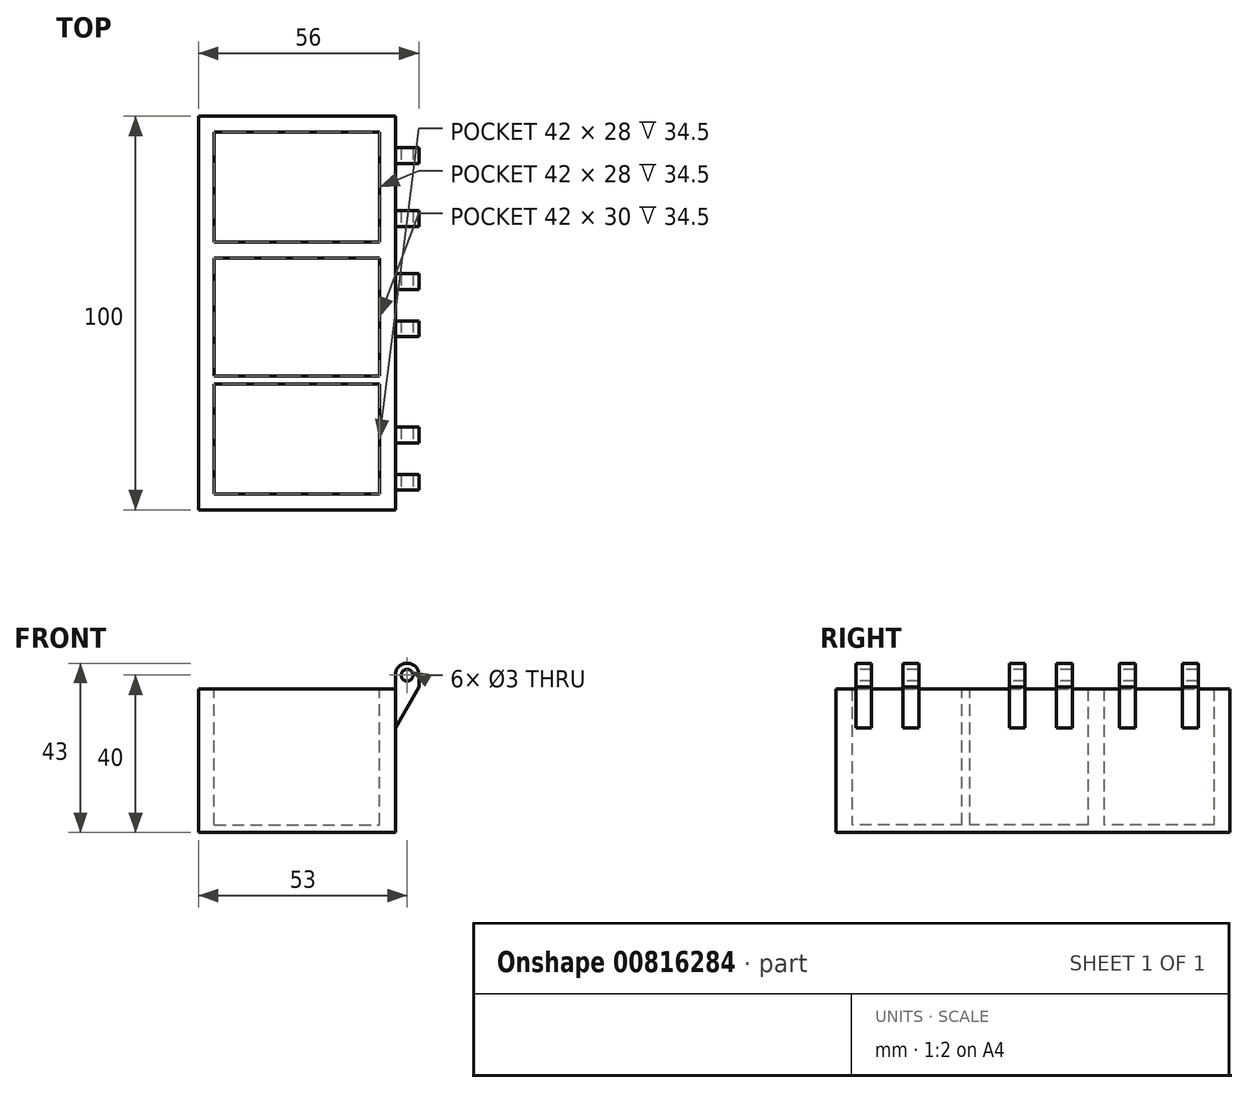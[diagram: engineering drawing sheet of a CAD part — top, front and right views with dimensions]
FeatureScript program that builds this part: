
annotation { "Feature Type Name" : "Feature", "Feature Type Description" : "" }
export const myFeature = defineFeature(function(context is Context, id is Id, definition is map)
    precondition{}
    {
        {
            var Q0;
            Q0=qCreatedBy(makeId("Top.planeOp"),FACE);
            var sketch = newSketch(context, id + "F0", { "sketchPlane" : qUnion([Q0])});
            skLineSegment(sketch, "E0.bottom", {"start": v(0, 0) * mm, "end": v(50, 0) * mm});
            skLineSegment(sketch, "E0.top", {"start": v(0, 100) * mm, "end": v(50, 100) * mm});
            skLineSegment(sketch, "E0.left", {"start": v(0, 0) * mm, "end": v(0, 100) * mm});
            skLineSegment(sketch, "E0.right", {"start": v(50, 0) * mm, "end": v(50, 100) * mm});
            skLineSegment(sketch, "E1.bottom", {"start": v(4, 96) * mm, "end": v(46, 96) * mm});
            skLineSegment(sketch, "E1.top", {"start": v(4, 68) * mm, "end": v(46, 68) * mm});
            skLineSegment(sketch, "E1.left", {"start": v(4, 96) * mm, "end": v(4, 68) * mm});
            skLineSegment(sketch, "E1.right", {"start": v(46, 96) * mm, "end": v(46, 68) * mm});
            skLineSegment(sketch, "E2.bottom", {"start": v(4, 64) * mm, "end": v(46, 64) * mm});
            skLineSegment(sketch, "E2.top", {"start": v(4, 4) * mm, "end": v(46, 4) * mm});
            skLineSegment(sketch, "E2.left", {"start": v(4, 64) * mm, "end": v(4, 4) * mm});
            skLineSegment(sketch, "E2.right", {"start": v(46, 64) * mm, "end": v(46, 4) * mm});
            skSolve(sketch);
        }
        {
            var Q0;
            Q0 = qSketchRegion(id + "F0", true);
            extrude(context, id + "F1", {"entities" : qUnion([Q0]), "depth" : 35 * mm, "offsetDistance" : 25 * mm});
        }
        {
            var Q0;
            Q0=makeQuery(id+"F1.opExtrude","CAP_FACE",FACE,{"disambiguationData":[OSD([sQuery(id+"F0.wireOp",EDGE,"E0.bottom"),sQuery(id+"F0.wireOp",EDGE,"E0.top"),sQuery(id+"F0.wireOp",EDGE,"E0.left"),sQuery(id+"F0.wireOp",EDGE,"E0.right"),sQuery(id+"F0.wireOp",EDGE,"E1.bottom"),sQuery(id+"F0.wireOp",EDGE,"E1.top"),sQuery(id+"F0.wireOp",EDGE,"E1.left"),sQuery(id+"F0.wireOp",EDGE,"E1.right"),sQuery(id+"F0.wireOp",EDGE,"E2.bottom"),sQuery(id+"F0.wireOp",EDGE,"E2.top"),sQuery(id+"F0.wireOp",EDGE,"E2.left"),sQuery(id+"F0.wireOp",EDGE,"E2.right")])],"isStart":true});
            var sketch = newSketch(context, id + "F2", { "sketchPlane" : qUnion([Q0])});
            skLineSegment(sketch, "E3.bottom", {"start": v(50, -100) * mm, "end": v(0, -100) * mm});
            skLineSegment(sketch, "E3.top", {"start": v(50, 0) * mm, "end": v(0, 0) * mm});
            skLineSegment(sketch, "E3.left", {"start": v(50, -100) * mm, "end": v(50, 0) * mm});
            skLineSegment(sketch, "E3.right", {"start": v(0, -100) * mm, "end": v(0, 0) * mm});
            skSolve(sketch);
        }
        {
            var Q0;
            Q0 = qSketchRegion(id + "F2", true);
            extrude(context, id + "F3", {"entities" : qUnion([Q0]), "operationType" : NewBodyOperationType.ADD, "depth" : 2 * mm, "offsetDistance" : 25 * mm});
        }
        {
            var Q0;
            Q0=makeQuery(id+"F3.boolean.opBoolean","MERGE",FACE,{"derivedFrom":[makeQuery(id+"F1.opExtrude","SWEPT_FACE",FACE,{"disambiguationData":[OSD([sQuery(id+"F0.wireOp",EDGE,"E0.bottom")])]}),makeQuery(id+"F3.opExtrude","SWEPT_FACE",FACE,{"disambiguationData":[OSD([sQuery(id+"F2.wireOp",EDGE,"E3.top")])]})]});
            var sketch = newSketch(context, id + "F4", { "sketchPlane" : qUnion([Q0])});
            skLineSegment(sketch, "E4", {"start": v(50, 24.6) * mm, "end": v(56, 35) * mm});
            skLineSegment(sketch, "E5", {"start": v(56, 35) * mm, "end": v(56, 41) * mm});
            skLineSegment(sketch, "E6", {"start": v(56, 41) * mm, "end": v(50, 41) * mm});
            skLineSegment(sketch, "E7", {"start": v(50, 41) * mm, "end": v(50, 35) * mm});
            skCircle(sketch, "E8", {"center": v(53, 38) * mm, "radius": 1.5 * mm});
            skLineSegment(sketch, "E9", {"start": v(50, 41) * mm, "end": v(56, 35) * mm, "construction": true});
            skLineSegment(sketch, "E10", {"start": v(50, 35) * mm, "end": v(56, 35) * mm, "construction": true});
            skSolve(sketch);
        }
        {
            var Q0;
            {var subQ1=sQuery(id+"F4.wireOp",EDGE,"E4");Q0=makeQuery(id+"F4.imprint","IMPRINT",FACE,{"disambiguationData":[TD([[makeQuery(id+"F4.imprint","IMPRINT",EDGE,{"derivedFrom":subQ1}),1.0]])]});}
            var Q1;
            Q1=makeQuery(id+"F3.boolean.opBoolean","MERGE",FACE,{"derivedFrom":[makeQuery(id+"F1.opExtrude","SWEPT_FACE",FACE,{"disambiguationData":[OSD([sQuery(id+"F0.wireOp",EDGE,"E0.top")])]}),makeQuery(id+"F3.opExtrude","SWEPT_FACE",FACE,{"disambiguationData":[OSD([sQuery(id+"F2.wireOp",EDGE,"E3.bottom")])]})]});
            extrude(context, id + "F5", {"entities" : qUnion([Q0]), "operationType" : NewBodyOperationType.ADD, "endBound" : BoundingType.UP_TO_SURFACE, "oppositeDirection" : true, "depth" : 25 * mm, "endBoundEntityFace" : qUnion([Q1]), "offsetDistance" : 25 * mm});
        }
        {
            var Q0;
            Q0=makeQuery(id+"F5.opExtrude","SWEPT_EDGE",EDGE,{"disambiguationData":[OSD([sQuery(id+"F4.wireOp",EDGE,"E5"),sQuery(id+"F4.wireOp",EDGE,"E6")])]});
            var Q1;
            Q1=makeQuery(id+"F5.opExtrude","SWEPT_EDGE",EDGE,{"disambiguationData":[OSD([sQuery(id+"F4.wireOp",EDGE,"E6"),sQuery(id+"F4.wireOp",EDGE,"E7")])]});
            fillet(context, id + "F6", {"entities" : qUnion([Q0, Q1]), "radius" : (5.7 / 2) * mm, "tangentPropagation" : true, "allowEdgeOverflow" : false});
        }
        {
            var Q0;
            Q0=makeQuery(id+"F3.opExtrude","CAP_FACE",FACE,{"disambiguationData":[OSD([sQuery(id+"F2.wireOp",EDGE,"E3.bottom"),sQuery(id+"F2.wireOp",EDGE,"E3.top"),sQuery(id+"F2.wireOp",EDGE,"E3.left"),sQuery(id+"F2.wireOp",EDGE,"E3.right")])],"isStart":false});
            var sketch = newSketch(context, id + "F7", { "sketchPlane" : qUnion([Q0])});
            skLineSegment(sketch, "E11.bottom", {"start": v(50, 0) * mm, "end": v(65, 0) * mm});
            skLineSegment(sketch, "E11.top", {"start": v(50, -5) * mm, "end": v(65, -5) * mm});
            skLineSegment(sketch, "E11.left", {"start": v(50, 0) * mm, "end": v(50, -5) * mm});
            skLineSegment(sketch, "E11.right", {"start": v(65, 0) * mm, "end": v(65, -5) * mm});
            skLineSegment(sketch, "E12.bottom", {"start": v(50, -21) * mm, "end": v(65, -21) * mm});
            skLineSegment(sketch, "E12.top", {"start": v(50, -44) * mm, "end": v(65, -44) * mm});
            skLineSegment(sketch, "E12.right", {"start": v(65, -21) * mm, "end": v(65, -44) * mm});
            skLineSegment(sketch, "E13.bottom", {"start": v(50, -60) * mm, "end": v(65, -60) * mm});
            skLineSegment(sketch, "E13.top", {"start": v(50, -72) * mm, "end": v(65, -72) * mm});
            skLineSegment(sketch, "E13.left", {"start": v(50, -60) * mm, "end": v(50, -72) * mm});
            skLineSegment(sketch, "E13.right", {"start": v(65, -60) * mm, "end": v(65, -72) * mm});
            skLineSegment(sketch, "E14.bottom", {"start": v(50, -100) * mm, "end": v(65, -100) * mm});
            skLineSegment(sketch, "E14.top", {"start": v(50, -92) * mm, "end": v(65, -92) * mm});
            skLineSegment(sketch, "E14.left", {"start": v(50, -100) * mm, "end": v(50, -92) * mm});
            skLineSegment(sketch, "E14.right", {"start": v(65, -100) * mm, "end": v(65, -92) * mm});
            skLineSegment(sketch, "E15.bottom", {"start": v(50, -88) * mm, "end": v(65, -88) * mm});
            skLineSegment(sketch, "E15.top", {"start": v(50, -76) * mm, "end": v(65, -76) * mm});
            skLineSegment(sketch, "E15.left", {"start": v(50, -88) * mm, "end": v(50, -76) * mm});
            skLineSegment(sketch, "E15.right", {"start": v(65, -88) * mm, "end": v(65, -76) * mm});
            skLineSegment(sketch, "E16.bottom", {"start": v(50, -56) * mm, "end": v(65, -56) * mm});
            skLineSegment(sketch, "E16.top", {"start": v(50, -48) * mm, "end": v(65, -48) * mm});
            skLineSegment(sketch, "E16.left", {"start": v(50, -56) * mm, "end": v(50, -48) * mm});
            skLineSegment(sketch, "E16.right", {"start": v(65, -56) * mm, "end": v(65, -48) * mm});
            skLineSegment(sketch, "E17.0", {"start": v(46, -96) * mm, "end": v(46, -68) * mm});
            skLineSegment(sketch, "E18.0.2", {"start": v(46, -68) * mm, "end": v(46, -96) * mm, "construction": true});
            skLineSegment(sketch, "E19", {"start": v(46, -82) * mm, "end": v(65, -82) * mm, "construction": true});
            skPoint(sketch, "E19.endSnap0", {"position": v(65, -82) * mm});
            skLineSegment(sketch, "E20.bottom", {"start": v(50, -9) * mm, "end": v(65, -9) * mm});
            skLineSegment(sketch, "E20.top", {"start": v(50, -17) * mm, "end": v(65, -17) * mm});
            skLineSegment(sketch, "E20.left", {"start": v(50, -9) * mm, "end": v(50, -17) * mm});
            skLineSegment(sketch, "E20.right", {"start": v(65, -9) * mm, "end": v(65, -17) * mm});
            skSolve(sketch);
        }
        {
            var Q0;
            Q0 = qSketchRegion(id + "F7", true);
            var Q1;
            {var subQ0=sQuery(id+"F7.wireOp",EDGE,"E12.bottom");Q1=makeQuery(id+"F7.imprint","IMPRINT",FACE,{"disambiguationData":[TD([[makeQuery(id+"F7.imprint","IMPRINT",EDGE,{"derivedFrom":subQ0}),-1.0]])]});}
            extrude(context, id + "F8", {"entities" : qUnion([Q0, Q1]), "operationType" : NewBodyOperationType.REMOVE, "oppositeDirection" : true, "depth" : 74.9 * mm, "offsetDistance" : 25 * mm});
        }
        {
            var Q0;
            Q0=makeQuery(id+"F1.opExtrude","CAP_FACE",FACE,{"disambiguationData":[OSD([sQuery(id+"F0.wireOp",EDGE,"E0.bottom"),sQuery(id+"F0.wireOp",EDGE,"E0.top"),sQuery(id+"F0.wireOp",EDGE,"E0.left"),sQuery(id+"F0.wireOp",EDGE,"E0.right"),sQuery(id+"F0.wireOp",EDGE,"E1.bottom"),sQuery(id+"F0.wireOp",EDGE,"E1.top"),sQuery(id+"F0.wireOp",EDGE,"E1.left"),sQuery(id+"F0.wireOp",EDGE,"E1.right"),sQuery(id+"F0.wireOp",EDGE,"E2.bottom"),sQuery(id+"F0.wireOp",EDGE,"E2.top"),sQuery(id+"F0.wireOp",EDGE,"E2.left"),sQuery(id+"F0.wireOp",EDGE,"E2.right")])],"isStart":false});
            var sketch = newSketch(context, id + "F9", { "sketchPlane" : qUnion([Q0])});
            skLineSegment(sketch, "E21.bottom", {"start": v(0, 0) * mm, "end": v(50, 0) * mm});
            skLineSegment(sketch, "E21.top", {"start": v(0, 100) * mm, "end": v(50, 100) * mm});
            skLineSegment(sketch, "E21.left", {"start": v(0, 0) * mm, "end": v(0, 100) * mm});
            skLineSegment(sketch, "E21.right", {"start": v(50, 0) * mm, "end": v(50, 100) * mm});
            skSolve(sketch);
        }
        {
            var Q0;
            {var subQ8=sQuery(id+"F9.wireOp",EDGE,"E21.bottom");Q0=makeQuery(id+"F9.imprint","IMPRINT",FACE,{"disambiguationData":[TD([[makeQuery(id+"F9.imprint","IMPRINT",EDGE,{"derivedFrom":subQ8}),1.0]])]});}
            extrude(context, id + "F10", {"entities" : qUnion([Q0]), "operationType" : NewBodyOperationType.REMOVE, "oppositeDirection" : true, "depth" : 0.5 * mm, "offsetDistance" : 25 * mm});
        }
        {
            var Q0;
            Q0=makeQuery(id+"F10.boolean.opBoolean","COPY",FACE,{"derivedFrom":makeQuery(id+"F10.opExtrude","CAP_FACE",FACE,{"disambiguationData":[OSD([sQuery(id+"F0.wireOp",EDGE,"E1.bottom"),sQuery(id+"F0.wireOp",EDGE,"E1.top"),sQuery(id+"F0.wireOp",EDGE,"E1.left"),sQuery(id+"F0.wireOp",EDGE,"E1.right"),sQuery(id+"F0.wireOp",EDGE,"E2.bottom"),sQuery(id+"F0.wireOp",EDGE,"E2.top"),sQuery(id+"F0.wireOp",EDGE,"E2.left"),sQuery(id+"F0.wireOp",EDGE,"E2.right"),sQuery(id+"F9.wireOp",EDGE,"E21.bottom"),sQuery(id+"F9.wireOp",EDGE,"E21.top"),sQuery(id+"F9.wireOp",EDGE,"E21.left"),sQuery(id+"F9.wireOp",EDGE,"E21.right")])],"isStart":false})});
            var sketch = newSketch(context, id + "F11", { "sketchPlane" : qUnion([Q0])});
            skLineSegment(sketch, "E22.bottom", {"start": v(4, 34) * mm, "end": v(46, 34) * mm});
            skLineSegment(sketch, "E22.top", {"start": v(4, 32) * mm, "end": v(46, 32) * mm});
            skLineSegment(sketch, "E22.left", {"start": v(4, 34) * mm, "end": v(4, 32) * mm});
            skLineSegment(sketch, "E22.right", {"start": v(46, 34) * mm, "end": v(46, 32) * mm});
            skSolve(sketch);
        }
        {
            var Q0;
            Q0=makeQuery(id+"F11.imprint","IMPRINT",FACE,{"disambiguationData":[TD([[makeQuery(id+"F11.imprint","IMPRINT",EDGE,{"derivedFrom":sQuery(id+"F11.wireOp",EDGE,"E22.bottom")}),-1.0]])]});
            var Q1;
            Q1=makeQuery(id+"F3.boolean.opBoolean","SPLIT",FACE,{"disambiguationData":[TD([makeQuery(id+"F1.opExtrude","SWEPT_FACE",FACE,{"disambiguationData":[OSD([sQuery(id+"F0.wireOp",EDGE,"E2.bottom")])]})])],"derivedFrom":makeQuery(id+"F3.opExtrude","CAP_FACE",FACE,{"disambiguationData":[OSD([sQuery(id+"F2.wireOp",EDGE,"E3.bottom"),sQuery(id+"F2.wireOp",EDGE,"E3.top"),sQuery(id+"F2.wireOp",EDGE,"E3.left"),sQuery(id+"F2.wireOp",EDGE,"E3.right")])],"isStart":true})});
            extrude(context, id + "F12", {"entities" : qUnion([Q0]), "operationType" : NewBodyOperationType.ADD, "endBound" : BoundingType.UP_TO_SURFACE, "oppositeDirection" : true, "depth" : 25 * mm, "endBoundEntityFace" : qUnion([Q1]), "offsetDistance" : 25 * mm});
        }
    });
